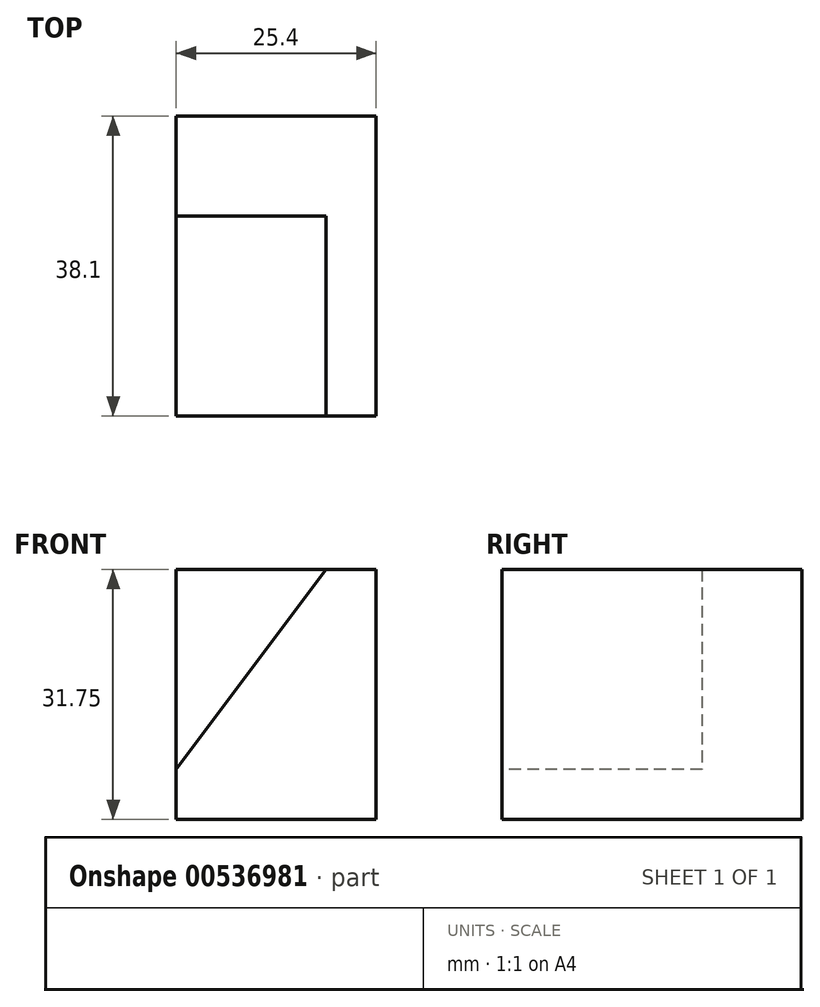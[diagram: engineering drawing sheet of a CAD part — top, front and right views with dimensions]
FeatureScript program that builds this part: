
annotation { "Feature Type Name" : "Feature", "Feature Type Description" : "" }
export const myFeature = defineFeature(function(context is Context, id is Id, definition is map)
    precondition{}
    {
        {
            var Q0;
            Q0=qCreatedBy(makeId("Front.planeOp"),FACE);
            var sketch = newSketch(context, id + "F0", { "sketchPlane" : qUnion([Q0])});
            skLineSegment(sketch, "E0", {"start": v(-62.1, 45.75) * mm, "end": v(-62.1, 14) * mm});
            skLineSegment(sketch, "E1", {"start": v(-62.1, 14) * mm, "end": v(-36.7, 14) * mm});
            skLineSegment(sketch, "E2", {"start": v(-36.7, 14) * mm, "end": v(-36.7, 45.75) * mm});
            skLineSegment(sketch, "E3", {"start": v(-36.7, 45.75) * mm, "end": v(-62.1, 45.75) * mm});
            skSolve(sketch);
        }
        {
            var Q0;
            Q0=makeQuery(id+"F0.imprint","IMPRINT",FACE,{"disambiguationData":[TD([[makeQuery(id+"F0.imprint","IMPRINT",EDGE,{"derivedFrom":sQuery(id+"F0.wireOp",EDGE,"E0")}),1.0]])]});
            extrude(context, id + "F1", {"entities" : qUnion([Q0]), "depth" : 38.1 * mm, "offsetDistance" : 25.4 * mm});
        }
        {
            var Q0;
            Q0=makeQuery(id+"F1.opExtrude","CAP_FACE",FACE,{"disambiguationData":[OSD([sQuery(id+"F0.wireOp",EDGE,"E0"),sQuery(id+"F0.wireOp",EDGE,"E1"),sQuery(id+"F0.wireOp",EDGE,"E2"),sQuery(id+"F0.wireOp",EDGE,"E3")])],"isStart":false});
            var sketch = newSketch(context, id + "F2", { "sketchPlane" : qUnion([Q0])});
            skLineSegment(sketch, "E4", {"start": v(-43.06, 45.75) * mm, "end": v(-62.1, 20.35) * mm});
            skSolve(sketch);
        }
        {
            var Q0;
            Q0 = qSketchRegion(id + "F2", true);
            var Q1;
            {var subQ0=sQuery(id+"F2.wireOp",EDGE,"E4");Q1=makeQuery(id+"F2.imprint","IMPRINT",FACE,{"disambiguationData":[TD([[makeQuery(id+"F2.imprint","IMPRINT",EDGE,{"derivedFrom":subQ0}),-1.0]])]});}
            extrude(context, id + "F3", {"entities" : qUnion([Q0, Q1]), "operationType" : NewBodyOperationType.REMOVE, "oppositeDirection" : true, "depth" : 25.4 * mm, "offsetDistance" : 25.4 * mm});
        }
    });
